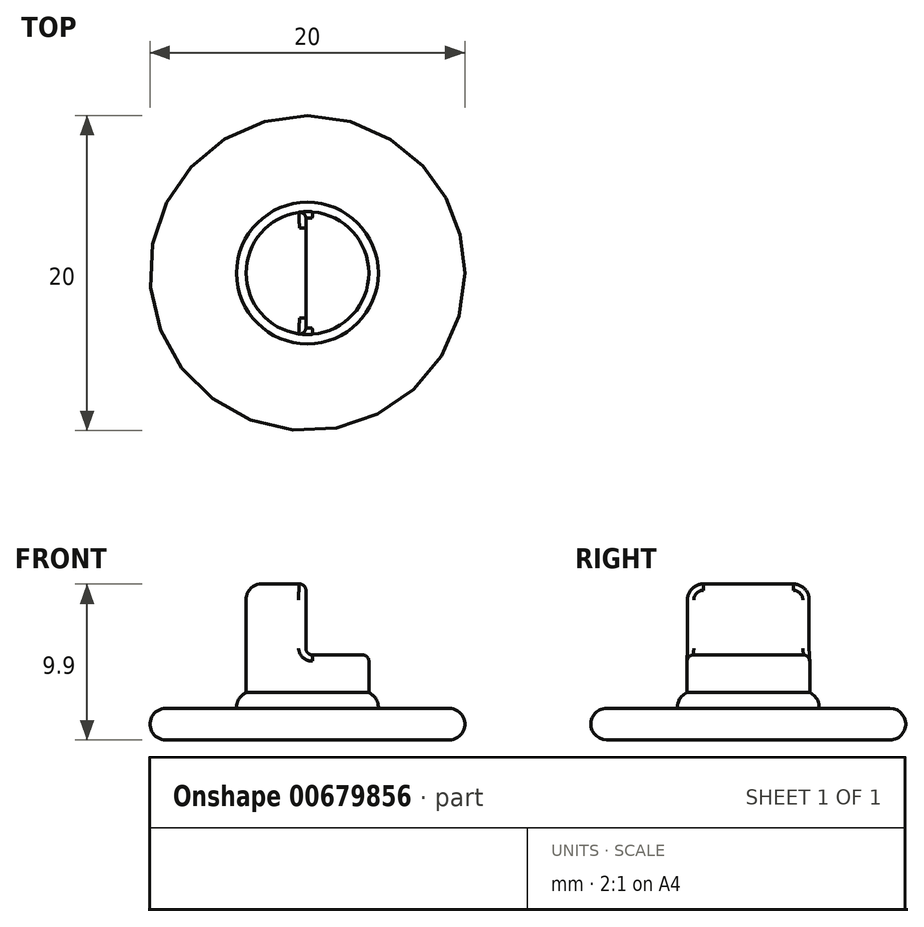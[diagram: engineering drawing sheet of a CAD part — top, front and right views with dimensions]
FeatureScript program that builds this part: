
annotation { "Feature Type Name" : "Feature", "Feature Type Description" : "" }
export const myFeature = defineFeature(function(context is Context, id is Id, definition is map)
    precondition{}
    {
        {
            var Q0;
            Q0=qCreatedBy(makeId("Top.planeOp"),FACE);
            var sketch = newSketch(context, id + "F0", { "sketchPlane" : qUnion([Q0])});
            skCircle(sketch, "E0", {"center": v(0, 0) * mm, "radius": 10 * mm});
            skSolve(sketch);
        }
        {
            var Q0;
            Q0 = qSketchRegion(id + "F0", true);
            extrude(context, id + "F1", {"entities" : qUnion([Q0]), "depth" : 2 * mm, "offsetDistance" : 25 * mm});
        }
        {
            var Q0;
            Q0=makeQuery(id+"F1.opExtrude","CAP_FACE",FACE,{"disambiguationData":[OSD([sQuery(id+"F0.wireOp",EDGE,"E0")])],"isStart":false});
            var sketch = newSketch(context, id + "F2", { "sketchPlane" : qUnion([Q0])});
            skCircle(sketch, "E1", {"center": v(0, 0) * mm, "radius": 4.5 * mm});
            skSolve(sketch);
        }
        {
            var Q0;
            Q0=makeQuery(id+"F2.imprint","IMPRINT",FACE,{"disambiguationData":[TD([[makeQuery(id+"F2.imprint","IMPRINT",EDGE,{"derivedFrom":sQuery(id+"F2.wireOp",EDGE,"E1")}),1.0]])]});
            extrude(context, id + "F3", {"entities" : qUnion([Q0]), "operationType" : NewBodyOperationType.ADD, "depth" : 1 * mm, "offsetDistance" : 25 * mm});
        }
        {
            var Q0;
            Q0=makeQuery(id+"F3.opExtrude","CAP_FACE",FACE,{"disambiguationData":[OSD([sQuery(id+"F2.wireOp",EDGE,"E1")])],"isStart":false});
            var sketch = newSketch(context, id + "F4", { "sketchPlane" : qUnion([Q0])});
            skCircle(sketch, "E2", {"center": v(0, 0) * mm, "radius": 3.9 * mm});
            skSolve(sketch);
        }
        {
            var Q0;
            Q0 = qSketchRegion(id + "F4", true);
            extrude(context, id + "F5", {"entities" : qUnion([Q0]), "operationType" : NewBodyOperationType.ADD, "depth" : 6.9 * mm, "offsetDistance" : 25 * mm});
        }
        {
            var Q0;
            Q0=makeQuery(id+"F5.opExtrude","CAP_FACE",FACE,{"disambiguationData":[OSD([sQuery(id+"F4.wireOp",EDGE,"E2")])],"isStart":false});
            cPlane(context, id + "F6", {"entities" : qUnion([Q0]), "cplaneType" : CPlaneType.OFFSET, "offset" : 1 * mm, "width" : 150 * mm, "height" : 150 * mm});
        }
        {
            var Q0;
            Q0=qCreatedBy(id+"F6.planeOp",FACE);
            var sketch = newSketch(context, id + "F7", { "sketchPlane" : qUnion([Q0])});
            skLineSegment(sketch, "E3.0", {"start": v(-0.1, 5.7) * mm, "end": v(-0.1, -5.6) * mm});
            skLineSegment(sketch, "E4", {"start": v(-0.1, 5.7) * mm, "end": v(5.14, 5.7) * mm});
            skLineSegment(sketch, "E5", {"start": v(5.14, 5.7) * mm, "end": v(5.14, -5.3) * mm});
            skLineSegment(sketch, "E6", {"start": v(5.14, -5.3) * mm, "end": v(-0.1, -5.6) * mm});
            skSolve(sketch);
        }
        {
            var Q0;
            Q0=makeQuery(id+"F7.imprint","IMPRINT",FACE,{"disambiguationData":[TD([[makeQuery(id+"F7.imprint","IMPRINT",EDGE,{"derivedFrom":sQuery(id+"F7.wireOp",EDGE,"E3.0")}),1.0]])]});
            extrude(context, id + "F8", {"entities" : qUnion([Q0]), "operationType" : NewBodyOperationType.REMOVE, "endBound" : BoundingType.SYMMETRIC, "depth" : 11 * mm, "offsetDistance" : 25 * mm});
        }
        {
            var Q0;
            Q0=makeQuery(id+"F1.opExtrude","CAP_EDGE",EDGE,{"disambiguationData":[OSD([sQuery(id+"F0.wireOp",EDGE,"E0")])],"isStart":true});
            var Q1;
            Q1=makeQuery(id+"F1.opExtrude","CAP_EDGE",EDGE,{"disambiguationData":[OSD([sQuery(id+"F0.wireOp",EDGE,"E0")])],"isStart":false});
            var Q2;
            Q2=makeQuery(id+"F3.opExtrude","CAP_EDGE",EDGE,{"disambiguationData":[OSD([sQuery(id+"F2.wireOp",EDGE,"E1")])],"isStart":false});
            var Q3;
            Q3=makeQuery(id+"F5.opExtrude","CAP_EDGE",EDGE,{"disambiguationData":[OSD([sQuery(id+"F4.wireOp",EDGE,"E2")])],"isStart":false});
            fillet(context, id + "F9", {"entities" : qUnion([Q0, Q1, Q2, Q3]), "radius" : 1 * mm, "tangentPropagation" : true, "allowEdgeOverflow" : false});
        }
        {
            var Q0;
            Q0=makeQuery(id+"F8.boolean.opBoolean","INTERSECT",EDGE,{"disambiguationData":[OD(0.0)],"derivedFrom":[makeQuery(id+"F5.opExtrude","SWEPT_FACE",FACE,{"disambiguationData":[OSD([sQuery(id+"F4.wireOp",EDGE,"E2")])]}),makeQuery(id+"F8.opExtrude","SWEPT_FACE",FACE,{"disambiguationData":[OSD([sQuery(id+"F7.wireOp",EDGE,"E3.0")])]})]});
            var Q1;
            Q1=makeQuery(id+"F9.opFillet","BLEND_EDGE",EDGE,{"disambiguationData":[OD(0.0)],"blendedFrom":[makeQuery(id+"F5.opExtrude","CAP_EDGE",EDGE,{"disambiguationData":[OSD([sQuery(id+"F4.wireOp",EDGE,"E2")])],"isStart":false}),makeQuery(id+"F8.boolean.opBoolean","COPY",FACE,{"derivedFrom":makeQuery(id+"F8.opExtrude","SWEPT_FACE",FACE,{"disambiguationData":[OSD([sQuery(id+"F7.wireOp",EDGE,"E3.0")])]})})],"blendedInto":[makeQuery(id+"F8.boolean.opBoolean","COPY",FACE,{"derivedFrom":makeQuery(id+"F8.opExtrude","SWEPT_FACE",FACE,{"disambiguationData":[OSD([sQuery(id+"F7.wireOp",EDGE,"E3.0")])]})})]});
            var Q2;
            Q2=makeQuery(id+"F8.boolean.opBoolean","INTERSECT",EDGE,{"derivedFrom":[makeQuery(id+"F5.opExtrude","CAP_FACE",FACE,{"disambiguationData":[OSD([sQuery(id+"F4.wireOp",EDGE,"E2")])],"isStart":false}),makeQuery(id+"F8.opExtrude","SWEPT_FACE",FACE,{"disambiguationData":[OSD([sQuery(id+"F7.wireOp",EDGE,"E3.0")])]})]});
            var Q3;
            Q3=makeQuery(id+"F9.opFillet","BLEND_EDGE",EDGE,{"disambiguationData":[OD(1.0)],"blendedFrom":[makeQuery(id+"F5.opExtrude","CAP_EDGE",EDGE,{"disambiguationData":[OSD([sQuery(id+"F4.wireOp",EDGE,"E2")])],"isStart":false}),makeQuery(id+"F8.boolean.opBoolean","COPY",FACE,{"derivedFrom":makeQuery(id+"F8.opExtrude","SWEPT_FACE",FACE,{"disambiguationData":[OSD([sQuery(id+"F7.wireOp",EDGE,"E3.0")])]})})],"blendedInto":[makeQuery(id+"F8.boolean.opBoolean","COPY",FACE,{"derivedFrom":makeQuery(id+"F8.opExtrude","SWEPT_FACE",FACE,{"disambiguationData":[OSD([sQuery(id+"F7.wireOp",EDGE,"E3.0")])]})})]});
            var Q4;
            Q4=makeQuery(id+"F8.boolean.opBoolean","INTERSECT",EDGE,{"disambiguationData":[OD(1.0)],"derivedFrom":[makeQuery(id+"F5.opExtrude","SWEPT_FACE",FACE,{"disambiguationData":[OSD([sQuery(id+"F4.wireOp",EDGE,"E2")])]}),makeQuery(id+"F8.opExtrude","SWEPT_FACE",FACE,{"disambiguationData":[OSD([sQuery(id+"F7.wireOp",EDGE,"E3.0")])]})]});
            var Q5;
            Q5=makeQuery(id+"F8.boolean.opBoolean","INTERSECT",EDGE,{"derivedFrom":[makeQuery(id+"F5.opExtrude","SWEPT_FACE",FACE,{"disambiguationData":[OSD([sQuery(id+"F4.wireOp",EDGE,"E2")])]}),makeQuery(id+"F8.opExtrude","CAP_FACE",FACE,{"disambiguationData":[OSD([sQuery(id+"F7.wireOp",EDGE,"E3.0"),sQuery(id+"F7.wireOp",EDGE,"E4"),sQuery(id+"F7.wireOp",EDGE,"E5"),sQuery(id+"F7.wireOp",EDGE,"E6")])],"isStart":true})]});
            var Q6;
            Q6=makeQuery(id+"F8.boolean.opBoolean","COPY",EDGE,{"derivedFrom":makeQuery(id+"F8.opExtrude","CAP_EDGE",EDGE,{"disambiguationData":[OSD([sQuery(id+"F7.wireOp",EDGE,"E3.0")])],"isStart":true})});
            fillet(context, id + "F10", {"entities" : qUnion([Q0, Q1, Q2, Q3, Q4, Q5, Q6]), "radius" : .4 * mm, "tangentPropagation" : true, "allowEdgeOverflow" : false});
        }
    });
